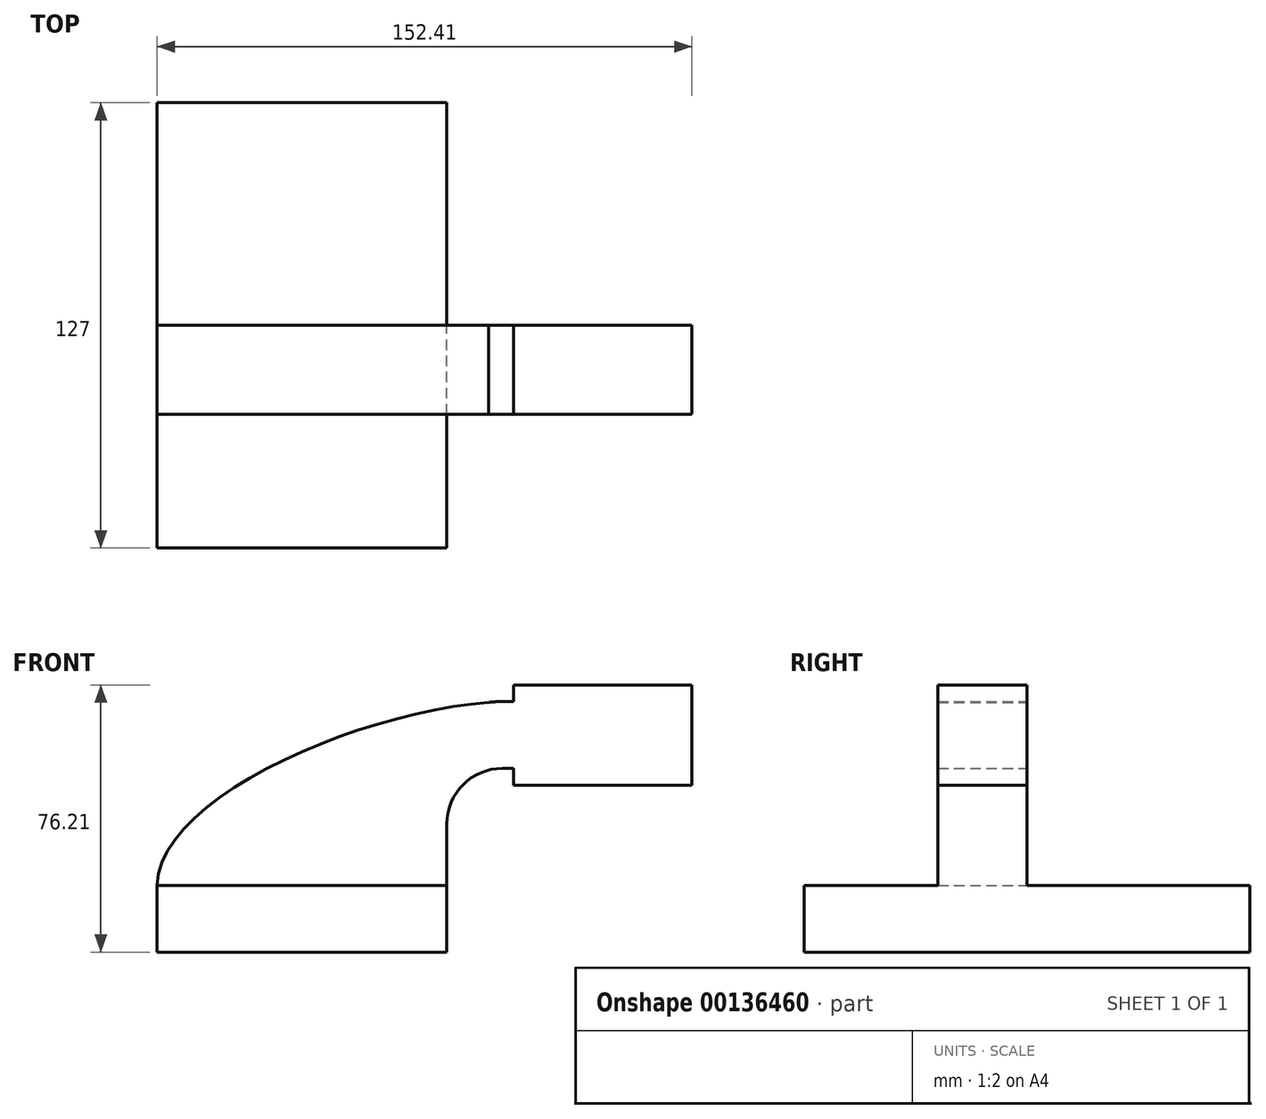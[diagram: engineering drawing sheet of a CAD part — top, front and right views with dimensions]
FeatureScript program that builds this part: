
annotation { "Feature Type Name" : "Feature", "Feature Type Description" : "" }
export const myFeature = defineFeature(function(context is Context, id is Id, definition is map)
    precondition{}
    {
        {
            var Q0;
            Q0=qCreatedBy(makeId("Front.planeOp"),FACE);
            var sketch = newSketch(context, id + "F0", { "sketchPlane" : qUnion([Q0])});
            skLineSegment(sketch, "E0.bottom", {"start": v(-41.28, 9.53) * mm, "end": v(41.28, 9.53) * mm});
            skLineSegment(sketch, "E0.top", {"start": v(-41.28, -9.53) * mm, "end": v(41.28, -9.53) * mm});
            skLineSegment(sketch, "E0.left", {"start": v(-41.28, 9.53) * mm, "end": v(-41.28, -9.52) * mm});
            skLineSegment(sketch, "E0.right", {"start": v(41.28, 9.53) * mm, "end": v(41.28, -9.52) * mm});
            skPoint(sketch, "E0.middle", {"position": v(0, 0) * mm});
            skLineSegment(sketch, "E1.bottom", {"start": v(111.12, 38.1) * mm, "end": v(60.32, 38.1) * mm});
            skLineSegment(sketch, "E1.top", {"start": v(111.12, 66.67) * mm, "end": v(60.32, 66.67) * mm});
            skLineSegment(sketch, "E1.left", {"start": v(111.12, 38.1) * mm, "end": v(111.12, 66.67) * mm});
            skLineSegment(sketch, "E1.right", {"start": v(60.32, 38.1) * mm, "end": v(60.32, 66.67) * mm});
            skPoint(sketch, "E1.middle", {"position": v(85.72, 52.39) * mm});
            skLineSegment(sketch, "E2", {"start": v(41.28, 9.53) * mm, "end": v(41.28, 27) * mm});
            skArc(sketch, "E3", {"start": v(41.27, 27) * mm, "mid": v(45.92, 38.23) * mm, "end": v(57.15, 42.88) * mm});
            skLineSegment(sketch, "E4", {"start": v(57.15, 42.88) * mm, "end": v(85.72, 42.88) * mm});
            skLineSegment(sketch, "E5.0", {"start": v(57.15, 61.93) * mm, "end": v(85.72, 61.93) * mm});
            skArc(sketch, "E5.1", {"start": v(22.23, 27) * mm, "mid": v(32.45, 51.7) * mm, "end": v(57.15, 61.93) * mm});
            skLineSegment(sketch, "E5.2", {"start": v(22.22, 9.53) * mm, "end": v(22.22, 27) * mm});
            skLineSegment(sketch, "E6", {"start": v(85.72, 38.1) * mm, "end": v(85.72, 66.67) * mm});
            skFitSpline(sketch, "E7", {"points": [v(57.15, 61.93) * mm, v(-41.28, 9.53) * mm], "startDerivative": vector(-110.08, -3.97) * mm, "endDerivative": vector(-1.85, -78.4) * mm});
            skSolve(sketch);
        }
        {
            var Q0;
            Q0=makeQuery(id+"F0.imprint","IMPRINT",FACE,{"disambiguationData":[TD([[makeQuery(id+"F0.imprint","IMPRINT",EDGE,{"derivedFrom":sQuery(id+"F0.wireOp",EDGE,"E0.top")}),1.0]])]});
            extrude(context, id + "F1", {"entities" : qUnion([Q0]), "endBound" : BoundingType.SYMMETRIC, "depth" : 127 * mm});
        }
        {
            var Q0;
            Q0 = qSketchRegion(id + "F0", true);
            extrude(context, id + "F2", {"entities" : qUnion([Q0]), "operationType" : NewBodyOperationType.ADD, "depth" : 25.4 * mm});
        }
    });
